# Revit family: NBS_INTRAMattingSystems_EntMatt_INTRAform-DMLowProfile
name_source: partatom
category: Generic Models
revit_build: Autodesk Revit 2013 (Build: 20121003_2115(x64)
units: mm (PartAtom-declared; Revit-internal decimal feet)

## types (1)
- INTRAform-DMLowProfile
    Arrangement = Interior inset or surface mounted.
    AssetType = Fixed
    BIMObjectName = NBS_INTRAMattingSystems_EntranceMatting_INTRAform-DMLowProfile
    BaseColour = Anodised to any RAL colour
    BaseMaterial = Aluminium
    Combustible = Yes
    Constituents = Aluminium plank system with choice of polyamide or polypropylene inserts.
    Construction = Closed
    Default Elevation = 0 mm  [stored 0 ft]
    Depth = 14 mm  [stored 0.0459318 ft]
    Description = Heavy duty 12mm aluminium matting system.
    DurationUnit = year
    EdgeTrimMaterial = NBS_Concept
    EntranceMattingMaterial = NBS_INTRAMattingSystems_EntranceMatting_INTRAform-DMLowProfile
    EnvironmentalProductDeclaration = 100% Recycled aluminium
    ExpectedLife = 10-15 years
    HasAntiStaticSurface = No
    HasNonSkidSurface = Yes
    IfcExportAs = IfcCoveringType
    IfcExportType = FLOORING
    InsertColourOptions = Elite polyamide - 608 Black, 607 Anthracite, 606 Grey, 602 Blue, 605 Brown, 609 Purple, 610 Turquoise, 604 Coco, 601 Red. Premier polyamide - 007 Anthracite, 014 Grey. Polypropylene - 443 Anthracite, 451 Grey.
    IntegralAccessories = Polypropylene ribbed fibre (colour)/ polyamide fibre (colour) / ribbed rubber/ brush – or combination of inserts.
    ManufacturerName = INTRAmatting Systems
    ManufacturerURL = www.intramatting.com
    MattingHeight = 11.5mm
    MatwellFrameFinish = Clear anodized as standard. Anodized finish in any RAL colour available to special order.
    MatwellFramingType = NBS_INTRAMattingSystems_EntranceMatting_Frame : 14mm
    ModelReference = INTRAform DM Low Profile
    ModuleWidth = 66.4mm
    NBSCertification = www.nationalbimlibrary.com/intramatting-systems/intraform-dm-low-profile
    NBSDescription = Entrance matting
    NBSReference = 45-35-35/420
    Name = EntranceMatting_INTRAform-DMLowProfile
    NominalHeight = 12 mm  [stored 0.0393701 ft]
    NominalLength = 0 mm  [stored 0 ft]
    NominalWidth = 0 mm  [stored 0 ft]
    ProductInformation = www.intramatting.com/downloads/IntraFORM_Low_Profile_Online_Brochure.pdf
    Shape = Rectangular
    SpacerMaterial = NBS_Concept
    SurfaceInsertOptions = Polyamide fibre, Polypropylene fibre.
    SustainabilityPerformance = Produced in the UK using 100% recycled aluminium and fully recylable inserts
    TemperatureResistance = Aluminium resistance: -50°C to +90°C.
    TotalThickness = 12 mm  [stored 0.0393701 ft]
    TrafficType = Heavy / Extreme
    Uniclass2 = 45-57-11/426
    Version = 1
    WarrantyDescription = 10 Performance Guarantee, subject to correct cleaning and maintenance procedures being carried out
    Weight = 12kg/m².

note: [stored X ft] marks values corroborated as IEEE doubles in the binary element streams (Revit-internal decimal feet)

## geometry (parser evidence)
native form markers: Sweep x3
no freeform markers — native parametric forms only
